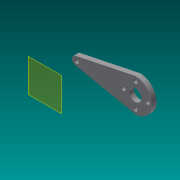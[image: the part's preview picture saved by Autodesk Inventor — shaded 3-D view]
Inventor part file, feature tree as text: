
AUTODESK INVENTOR PART (.ipt)
format: ipt  version: 2013 SP2 (Build 170200200, 200)  size: 140,800 bytes
history: native  units: in
note: dims shown in document units (in); Inventor stores cm internally (conversion verified against a paired STEP export)
features: sheet_metal_op x5, sketch x4, other x3, plane x1
ambient origin geometry x8: Origin, YZ Plane, XZ Plane, XY Plane, X Axis, Y Axis, Z Axis, Center Point
bodies: Solid1 (feature_tree)
feature tree (13):
  sheet_metal_op  "Face1"
  sheet_metal_op  "Face2"
  sheet_metal_op  "Face3"
  sketch  "Sketch4"  dims[d4=0.125in d5=0.0625in d6=0.25in d7=0.125in d8=0.0787in d9=0.0787in d10=0.0787in d11=0.0787in d12=0.125in d13=0.125in d14=0.0625in d15=0.25in d16=0.125in d17=0.0787in]
  sketch  "Sketch1"  dims[d1=0.118in]
  other  "Plate1"
  plane  "Work Plane2"
  sketch  "Sketch2"  dims[d2=0.125in]
  other  "Plate2"
  sheet_metal_op  "Bend1"
  sketch  "Sketch3"  dims[d3=0.125in]
  other  "Plate3"
  sheet_metal_op  "Bend2"
